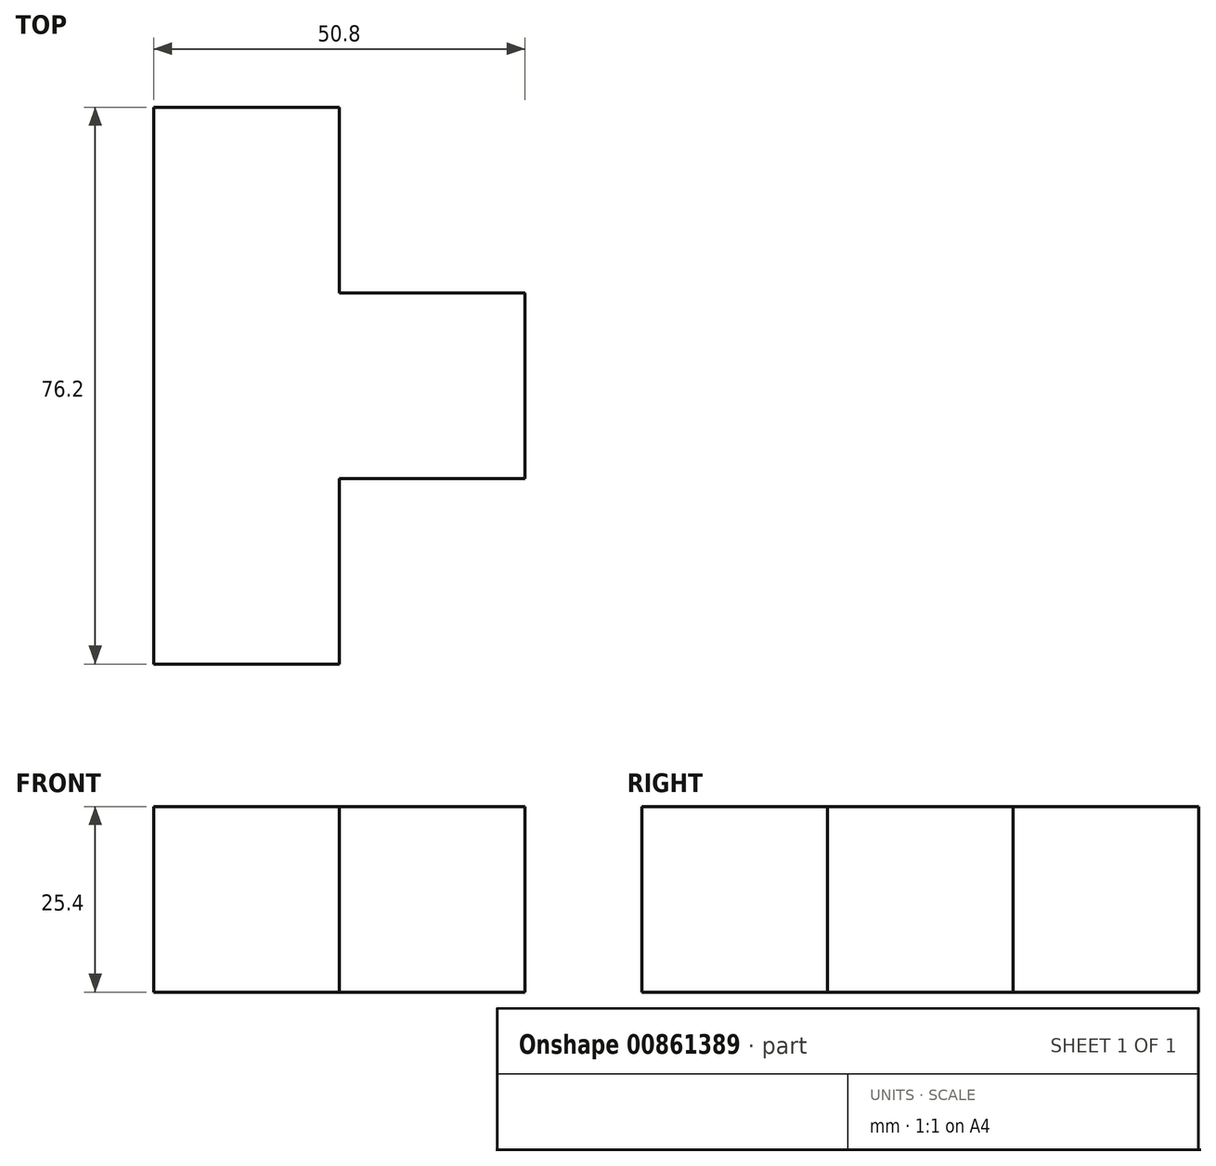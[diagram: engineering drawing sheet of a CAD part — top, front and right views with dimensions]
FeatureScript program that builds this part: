
annotation { "Feature Type Name" : "Feature", "Feature Type Description" : "" }
export const myFeature = defineFeature(function(context is Context, id is Id, definition is map)
    precondition{}
    {
        {
            var Q0;
            Q0=qCreatedBy(makeId("Top.planeOp"),FACE);
            var sketch = newSketch(context, id + "F0", { "sketchPlane" : qUnion([Q0])});
            skLineSegment(sketch, "E0.bottom", {"start": v(12.7, -38.1) * mm, "end": v(-12.7, -38.1) * mm});
            skLineSegment(sketch, "E0.top", {"start": v(12.7, 38.1) * mm, "end": v(-12.7, 38.1) * mm});
            skLineSegment(sketch, "E0.left", {"start": v(12.7, -38.1) * mm, "end": v(12.7, 38.1) * mm});
            skLineSegment(sketch, "E0.right", {"start": v(-12.7, -38.1) * mm, "end": v(-12.7, 38.1) * mm});
            skPoint(sketch, "E0.middle", {"position": v(0, 0) * mm});
            skSolve(sketch);
        }
        {
            var Q0;
            Q0 = qSketchRegion(id + "F0", true);
            extrude(context, id + "F1", {"entities" : qUnion([Q0]), "depth" : 25.4 * mm, "offsetDistance" : 25.4 * mm});
        }
        {
            var Q0;
            Q0=makeQuery(id+"F1.opExtrude","SWEPT_FACE",FACE,{"disambiguationData":[OSD([sQuery(id+"F0.wireOp",EDGE,"E0.left")])]});
            var sketch = newSketch(context, id + "F2", { "sketchPlane" : qUnion([Q0])});
            skLineSegment(sketch, "E1.bottom", {"start": v(12.7, 25.4) * mm, "end": v(-12.7, 25.4) * mm});
            skLineSegment(sketch, "E1.top", {"start": v(12.7, 0) * mm, "end": v(-12.7, 0) * mm});
            skLineSegment(sketch, "E1.left", {"start": v(12.7, 25.4) * mm, "end": v(12.7, 0) * mm});
            skLineSegment(sketch, "E1.right", {"start": v(-12.7, 25.4) * mm, "end": v(-12.7, 0) * mm});
            skLineSegment(sketch, "E2", {"start": v(0, 25.4) * mm, "end": v(0, 0) * mm});
            skSolve(sketch);
        }
        {
            var Q0;
            Q0 = qSketchRegion(id + "F2", true);
            extrude(context, id + "F3", {"entities" : qUnion([Q0]), "operationType" : NewBodyOperationType.ADD, "depth" : 25.4 * mm, "offsetDistance" : 25.4 * mm});
        }
    });
